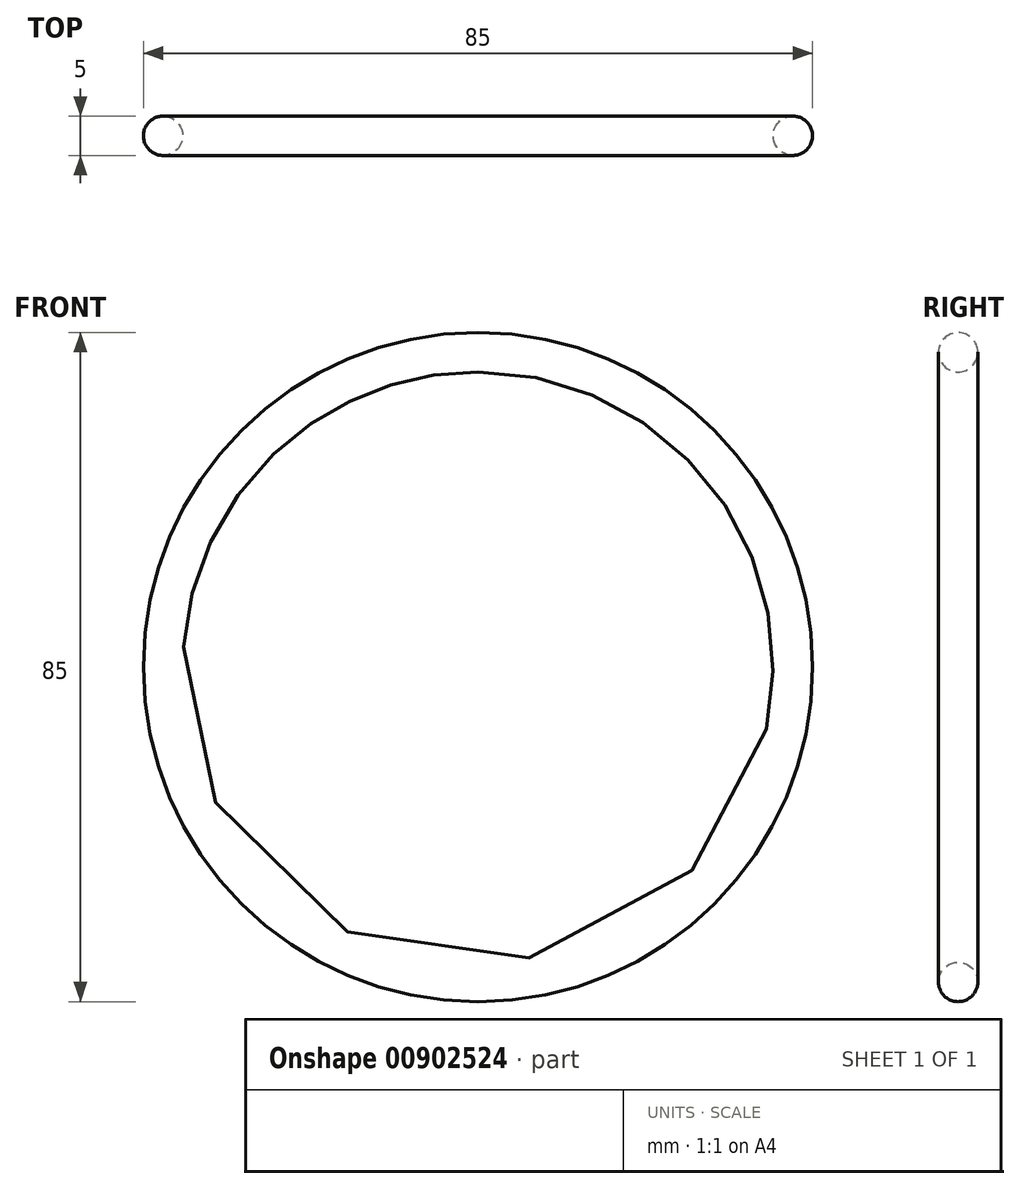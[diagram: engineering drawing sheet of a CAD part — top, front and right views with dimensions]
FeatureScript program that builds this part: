
annotation { "Feature Type Name" : "Feature", "Feature Type Description" : "" }
export const myFeature = defineFeature(function(context is Context, id is Id, definition is map)
    precondition{}
    {
        {
            var Q0;
            Q0=qCreatedBy(makeId("Front.planeOp"),FACE);
            var sketch = newSketch(context, id + "F0", { "sketchPlane" : qUnion([Q0])});
            skCircle(sketch, "E0", {"center": v(0, 0) * mm, "radius": 40 * mm});
            skSolve(sketch);
        }
        {
            var Q0;
            Q0=qCreatedBy(makeId("Right.planeOp"),FACE);
            var sketch = newSketch(context, id + "F1", { "sketchPlane" : qUnion([Q0])});
            skCircle(sketch, "E1", {"center": v(0, 40) * mm, "radius": 2.5 * mm});
            skLineSegment(sketch, "E2", {"start": v(48.88, 0) * mm, "end": v(-48.88, 0) * mm, "construction": true});
            skSolve(sketch);
        }
        {
            var Q0;
            Q0=makeQuery(id+"F1.imprint","IMPRINT",FACE,{"disambiguationData":[TD([[makeQuery(id+"F1.imprint","IMPRINT",EDGE,{"derivedFrom":sQuery(id+"F1.wireOp",EDGE,"E1")}),1.0]])]});
            var Q1;
            Q1=sQuery(id+"F1.wireOp",EDGE,"E2");
            revolve(context, id + "F2", {"surfaceOperationType" : NewSurfaceOperationType.NEW, "entities" : qUnion([Q0]), "axis" : qUnion([Q1]), "revolveType" : RevolveType.FULL});
        }
    });
